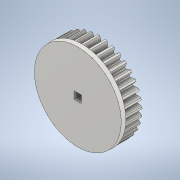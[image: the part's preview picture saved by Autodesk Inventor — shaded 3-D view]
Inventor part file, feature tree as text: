
AUTODESK INVENTOR PART (.ipt)
format: ipt  version: 2022 (Build 260153000, 153)  size: 1,325,056 bytes
history: native  units: mm (DEFAULTED — no unit token found)
features: sketch x4, extrude x3, plane x3, other x3, chamfer x1, revolve x1, projected_geometry x1
ambient origin geometry x8: Origin, YZ Plane, XZ Plane, XY Plane, X Axis, Y Axis, Z Axis, Center Point
bodies: Solid1 (feature_tree)
feature tree (16):
  extrude  "Extrusion1"  Depth=9.525mm TaperAngle=0.0deg
  plane  "Work Plane1"
  plane  "Work Plane2"
  plane  "Work Plane3"
  other  "Spur Gear"
  extrude  "Extrusion2"  Depth=76.2mm TaperAngle=0.0deg
  extrude  "Extrusion3"  TaperAngle=0.0deg  [1 undecoded]
  chamfer  "Chamfer1"  Distance=23.75408mm
  revolve  "Revolution1"  [1 undecoded]
  sketch  "Sketch1"  dims[d0=39.50816mm d1=9.525mm d2=0.0mm]
  sketch  "Sketch2"  dims[d3=37.0mm d4=76.2mm d5=0.0mm]
  other  "Srf1"
  sketch  "Sketch3"  dims[d6=0.0mm d7=0.849079mm d9=0.0mm d14=0.0mm d15=23.75408mm]
  sketch  "Sketch4"  dims[d16=0.0mm d17=0.0mm d18=0.0mm d19=23.75408mm d20=3.325mm d21=0.0mm d22=0.0mm d23=12.1mm d24=1.5875mm d25=0.0mm d26=1.5875mm d27=3.175mm d28=45.0deg d29=35.0mm d30=6.35mm d32=9.525mm d33=39.5mm d34=360.0deg d35=1.2mm d36=14.835299mm]
  projected_geometry  "Projected Loop1"
  other  "Pitch Diameter"
note: 2 required parameter values undecoded (feature->parameter linkage not recoverable at this tier; creation-order binding heuristic only, values carry confidence <= 0.55)